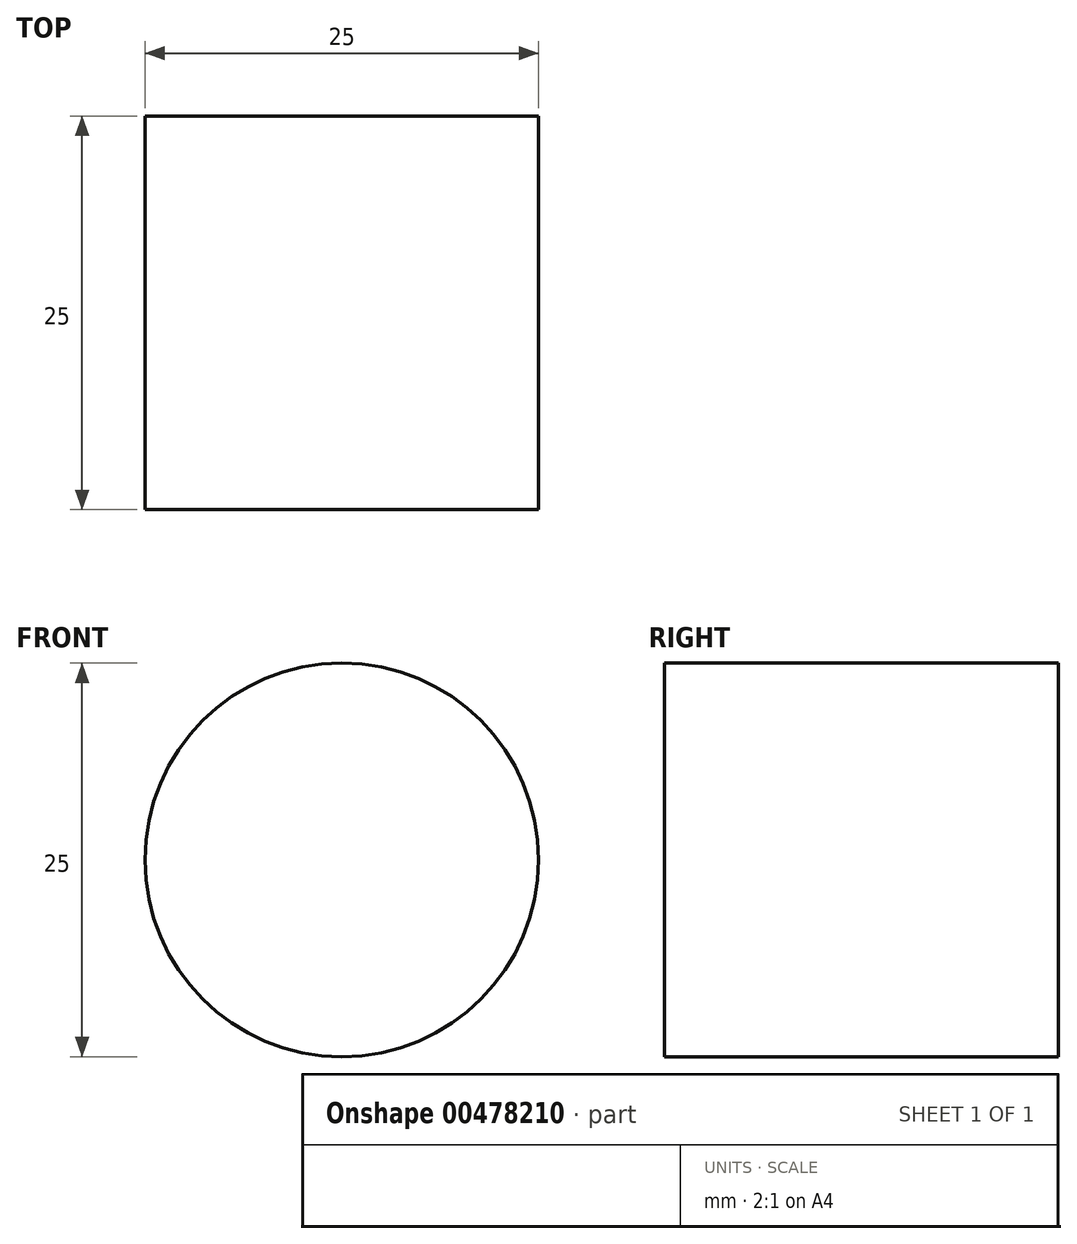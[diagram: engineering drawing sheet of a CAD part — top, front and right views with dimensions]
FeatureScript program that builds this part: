
annotation { "Feature Type Name" : "Feature", "Feature Type Description" : "" }
export const myFeature = defineFeature(function(context is Context, id is Id, definition is map)
    precondition{}
    {
        {
            var Q0;
            Q0=qCreatedBy(makeId("Front.planeOp"),FACE);
            var sketch = newSketch(context, id + "F0", { "sketchPlane" : qUnion([Q0])});
            skCircle(sketch, "E0", {"center": v(0, 0) * mm, "radius": 12.5 * mm});
            skSolve(sketch);
        }
        {
            var Q0;
            Q0=makeQuery(id+"F0.imprint","IMPRINT",FACE,{"disambiguationData":[TD([[makeQuery(id+"F0.imprint","IMPRINT",EDGE,{"derivedFrom":sQuery(id+"F0.wireOp",EDGE,"E0")}),1.0]])]});
            extrude(context, id + "F1", {"entities" : qUnion([Q0]), "depth" : 25 * mm});
        }
    });
